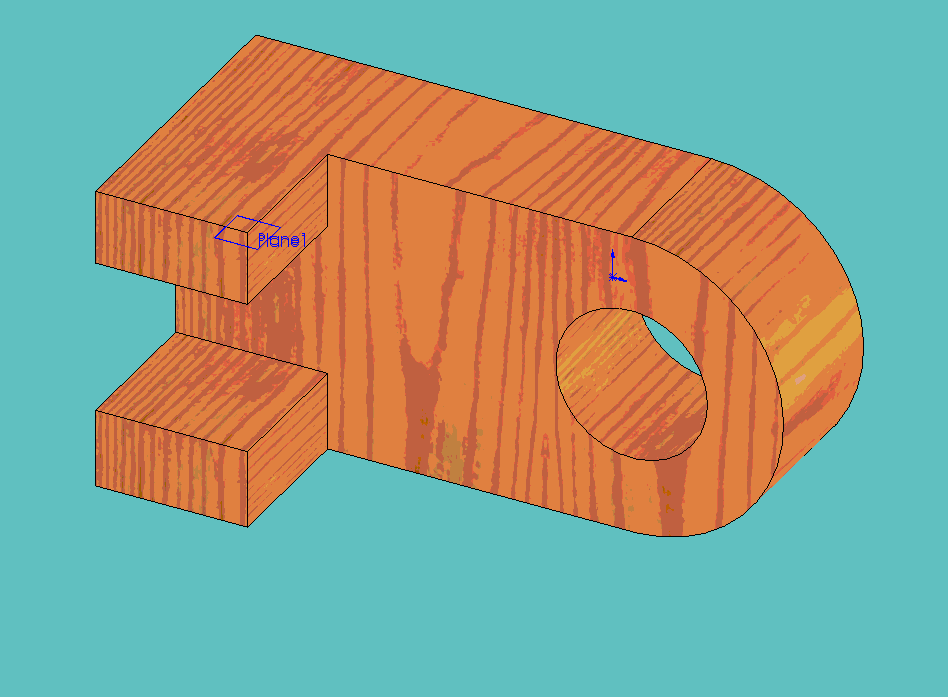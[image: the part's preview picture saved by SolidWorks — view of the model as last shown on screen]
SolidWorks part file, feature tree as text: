
SOLIDWORKS PART (.sldprt)
format: sldprt  version: not decoded by parser v0  size: 189,440 bytes
history: native  units: mm
features: plane x4, sketch x4, extrude x2, cut_extrude x2, material x1 (+10 scaffold rows collapsed)
feature tree (23):
  scaffold x10  (default folders/planes/origin — collapsed)
  material  "Cedar"
  plane  "Frontal"
  plane  "Horizontal"
  plane  "Profile"
  sketch  "Sketch2"  dims[D1=101.6mm D2=101.6mm D3=~179.546381mm]
  extrude  "Extrude1"  Depth=50.8mm
  sketch  "Sketch3"  dims[D1=50.8mm D2=0.0mm]
  extrude  "Extrude2"  Depth=50.8mm
  plane  "Plane1"
  sketch  "Sketch5"  dims[D1=50.8mm]
  cut_extrude  "Cut-Extrude1"  Depth=50.8mm
  sketch  "Sketch6"  dims[D1=~30.512757mm]
  cut_extrude  "Cut-Extrude2"  [1 undecoded]
decode coverage: 7 of 8 modeling features carry decoded parameters
note: ~ marks probable driven/reference dimensions
note: 1 parameter value undecoded
note: suppression state not decoded; provenance and decode notes live in map.json
